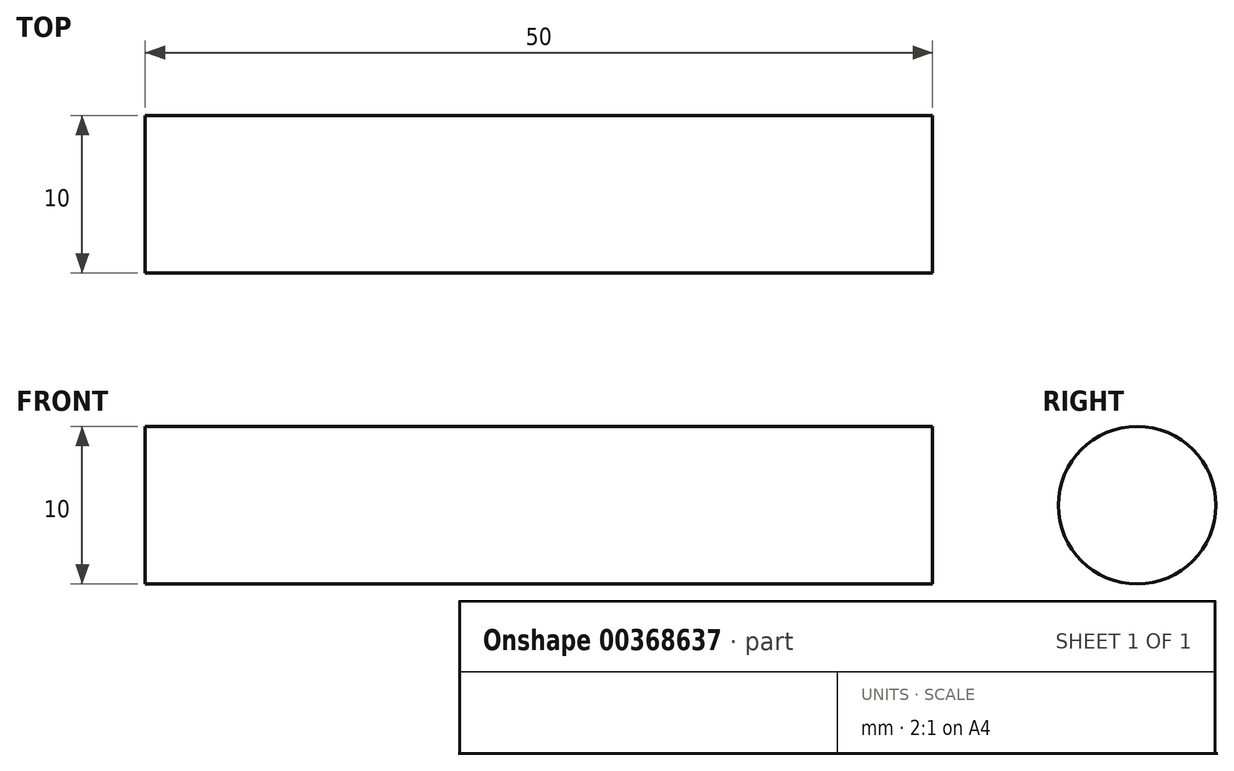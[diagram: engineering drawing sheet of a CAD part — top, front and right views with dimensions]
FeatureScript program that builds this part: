
annotation { "Feature Type Name" : "Feature", "Feature Type Description" : "" }
export const myFeature = defineFeature(function(context is Context, id is Id, definition is map)
    precondition{}
    {
        {
            var Q0;
            Q0=qCreatedBy(makeId("Right.planeOp"),FACE);
            var sketch = newSketch(context, id + "F0", { "sketchPlane" : qUnion([Q0])});
            skCircle(sketch, "E0", {"center": v(0, 0) * mm, "radius": 5 * mm});
            skSolve(sketch);
        }
        {
            var Q0;
            Q0 = qSketchRegion(id + "F0", true);
            extrude(context, id + "F1", {"entities" : qUnion([Q0]), "depth" : 25 * mm});
        }
        {
            var Q0;
            Q0=makeQuery(id+"F1.opExtrude","CAP_FACE",FACE,{"disambiguationData":[OSD([sQuery(id+"F0.wireOp",EDGE,"E0")])],"isStart":false});
            extrude(context, id + "F2", {"entities" : qUnion([Q0]), "operationType" : NewBodyOperationType.ADD, "depth" : 25 * mm});
        }
    });
